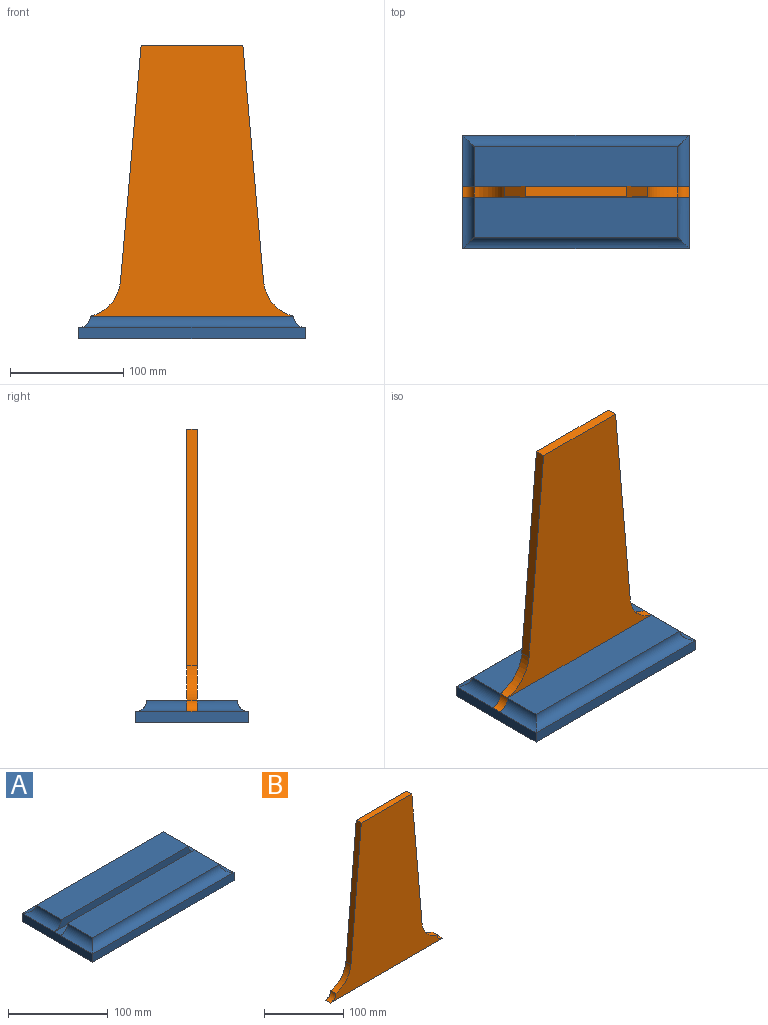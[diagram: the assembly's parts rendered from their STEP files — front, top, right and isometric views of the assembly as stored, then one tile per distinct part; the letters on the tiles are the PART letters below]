
ASSEMBLY  parts=2 mates=1
PART A: 16 faces, bbox 200x100x20 mm
  f0: plane 180x35.5mm, normal (0,0,1), area 6390mm2, adj f1,f8,f12,f14
  f1: cylinder r=10mm len=200mm, axis (-1,0,0), area 2941.6mm2, adj f0,f9,f12,f14
  f2: cylinder r=10mm len=200mm, axis (-1,0,0), area 2941.6mm2, adj f3,f11,f13,f15
  f3: plane 180x35.5mm, normal (0,0,1), area 6390mm2, adj f2,f6,f13,f15
  f4: plane 100x10mm, normal (1,0,0), area 1000mm2, adj f7,f9,f10,f11,f14,f15
  f5: plane 100x10mm, normal (-1,0,0), area 1000mm2, adj f7,f9,f10,f11,f12,f13
  f6: plane 200x10mm, normal (0,-1,0), area 1842.9mm2, adj f3,f7,f13,f15
  f7: plane 200x9mm, normal (0,0,1), area 1800mm2, adj f4,f5,f6,f8
  f8: plane 200x10mm, normal (0,1,0), area 1842.9mm2, adj f0,f7,f12,f14
  f9: plane 200x10mm, normal (0,-1,0), area 2000mm2, adj f1,f4,f5,f10
  f10: plane 200x100mm, normal (0,0,-1), area 20000mm2, adj f4,f5,f9,f11
  f11: plane 200x10mm, normal (0,1,0), area 2000mm2, adj f2,f4,f5,f10
  f12: cylinder r=10mm len=45.5mm, axis (0,1,0), area 614.7mm2, adj f0,f1,f5,f8
  f13: cylinder r=10mm len=45.5mm, axis (0,1,0), area 614.7mm2, adj f2,f3,f5,f6
  f14: cylinder r=10mm len=45.5mm, axis (0,1,0), area 614.7mm2, adj f0,f1,f4,f8
  f15: cylinder r=10mm len=45.5mm, axis (0,1,0), area 614.7mm2, adj f2,f3,f4,f6
PART B: 10 faces, bbox 200x9x250 mm
  f0: plane 90x9mm, normal (0,0,1), area 810mm2, adj f1,f5,f6,f7
  f1: plane 209.01x18.29mm, normal (-1,0,0.09), area 1888.3mm2, adj f0,f2,f5,f6
  f2: cylinder r=35mm len=30.99mm, axis (0,1,0), area 393.3mm2, adj f1,f3,f5,f6
  f3: cylinder r=10mm len=10mm, axis (0,1,0), area 141.4mm2, adj f2,f4,f5,f6
  f4: plane 200x9mm, normal (0,0,-1), area 1800mm2, adj f3,f5,f6,f9
  f5: plane 250x200mm, normal (0,-1,0), area 28858.6mm2, adj f0,f1,f2,f3,f4,f7,f8,f9
  f6: plane 250x200mm, normal (0,1,0), area 28858.6mm2, adj f0,f1,f2,f3,f4,f7,f8,f9
  f7: plane 209.01x18.29mm, normal (1,0,0.09), area 1888.3mm2, adj f0,f5,f6,f8
  f8: cylinder r=35mm len=30.99mm, axis (0,1,0), area 393.3mm2, adj f5,f6,f7,f9
  f9: cylinder r=10mm len=10mm, axis (0,1,0), area 141.4mm2, adj f4,f5,f6,f8
PLACE A at identity
PLACE B t=(0,0,10)mm
MATE fastened B.f4 <-> A.f7  axis (0,0,-1) through (0,0,10)mm
